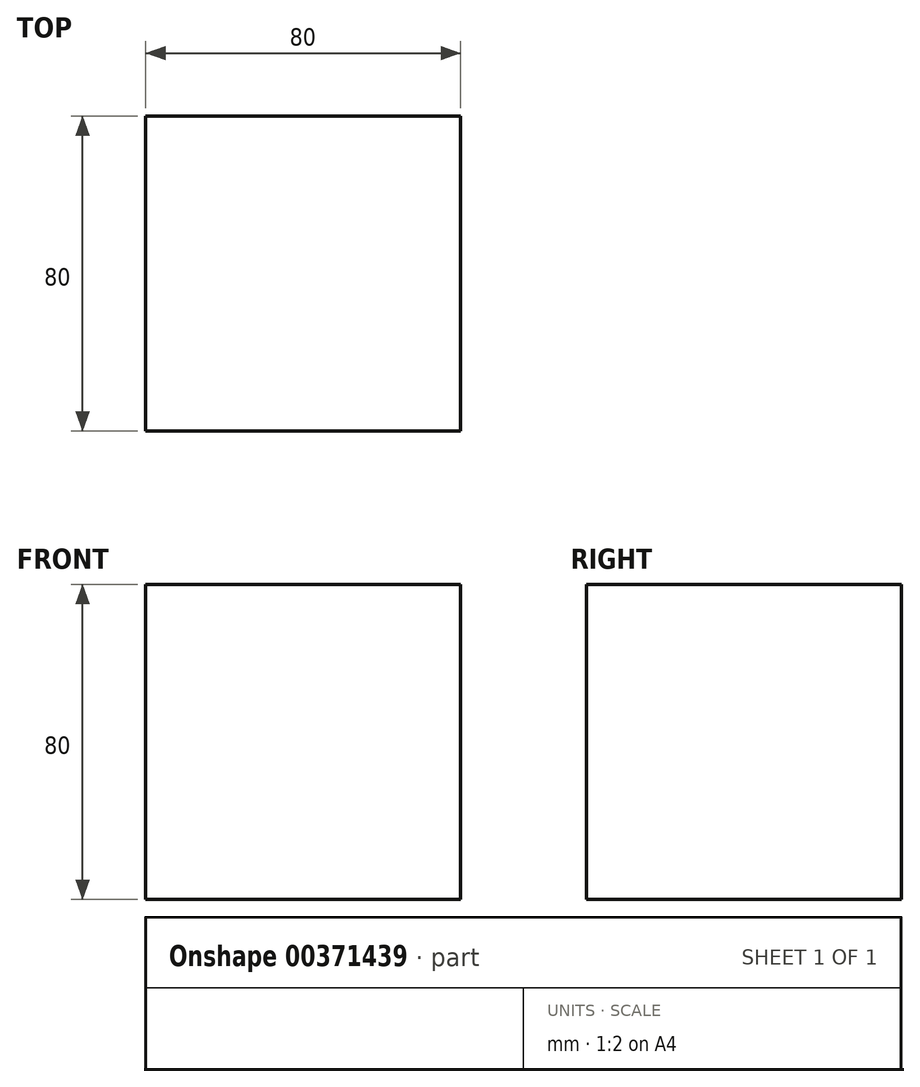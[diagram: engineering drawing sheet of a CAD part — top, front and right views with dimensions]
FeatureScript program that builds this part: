
annotation { "Feature Type Name" : "Feature", "Feature Type Description" : "" }
export const myFeature = defineFeature(function(context is Context, id is Id, definition is map)
    precondition{}
    {
        {
            var Q0;
            Q0=qCreatedBy(makeId("Top.planeOp"),FACE);
            var sketch = newSketch(context, id + "F0", { "sketchPlane" : qUnion([Q0])});
            skLineSegment(sketch, "E0.bottom", {"start": v(-44.12, 45.26) * mm, "end": v(35.88, 45.26) * mm});
            skLineSegment(sketch, "E0.top", {"start": v(-44.12, -34.74) * mm, "end": v(35.88, -34.74) * mm});
            skLineSegment(sketch, "E0.left", {"start": v(-44.12, 45.26) * mm, "end": v(-44.12, -34.74) * mm});
            skLineSegment(sketch, "E0.right", {"start": v(35.88, 45.26) * mm, "end": v(35.88, -34.74) * mm});
            skSolve(sketch);
        }
        {
            var Q0;
            Q0 = qSketchRegion(id + "F0", true);
            extrude(context, id + "F1", {"entities" : qUnion([Q0]), "depth" : 80 * mm});
        }
    });
